# Revit family: Domotics-SerieCivili-GEWISS-27COMBI_SYSTEM-IP44_PRESE_IEC309
name_source: partatom
category: Modelli generici
revit_build: Autodesk Revit 2016 (Build: 20161004_0715(x64)
units: mm (PartAtom-declared; Revit-internal decimal feet)

## family parameters
Condiviso = No
Host = Muro
Punto di calcolo locali = No
Può ospitare armatura = No
Quota connettore circolare = Usa diametro
Sempre verticale = Sì
Taglio con vuoti quando caricato = No
Tipo di parte = Normale

## types (2) — shared parameters
Altezza = 84 mm
Catalogo = DOMOTICS
Catalogo Serie = 27COMBI
Classe isolamento = II
Codice Electrocod = 2210
Colore = Grigio RAL 7035
Corrente nominale (In) = 16
Dim. esterne BxHxP (mm) = 116x90x45
Finitura = <Per categoria>
Glow Wire Test = 650°C
Grado di protezione = IP44
IDF = aa8affc8-fe2d-4bcd-bf8c-913abe223fa2
IDT = f00df10a-2b06-41cb-b6d5-a9cceb99cd24
Immagine tipo = GW26421.jpg
Larghezza = 116 mm  [stored 0.380577 ft]
Norma di riferimento = IEC 309
Produttore = GEWISS S.p.A.
Profondità = 45 mm  [stored 0.147638 ft]
Riferimento h = 6
Scheda Tecnica = https://www.gewiss.com
Temperatura di installazione = -25 +60 °C
Termopressione con biglia = 70 °C
URL = https://www.gewiss.com
Versione file RFA = 18.0
leva = <Per categoria>

## per-type parameters (varying)
| type | Codice EAN | Descrizione | Modello | Numero poli | Tensione nominale |
| GW26421 - Presa IEC309 3P+T 16A 380V IP44 incasso | 8011564025431 | PRESA IEC309 3P+T 16A 380V IP44 INCASSO | GW26421 | 3P+T | 400 V ac |
| GW26420 - Presa IEC309 2P+T 16A 220V IP44 incasso | 8011564025448 | PRESA IEC309 2P+T 16A 220V IP44 INCASSO | GW26420 | 2P+T | 230 V ac |

note: [stored X ft] marks values corroborated as IEEE doubles in the binary element streams (Revit-internal decimal feet)
